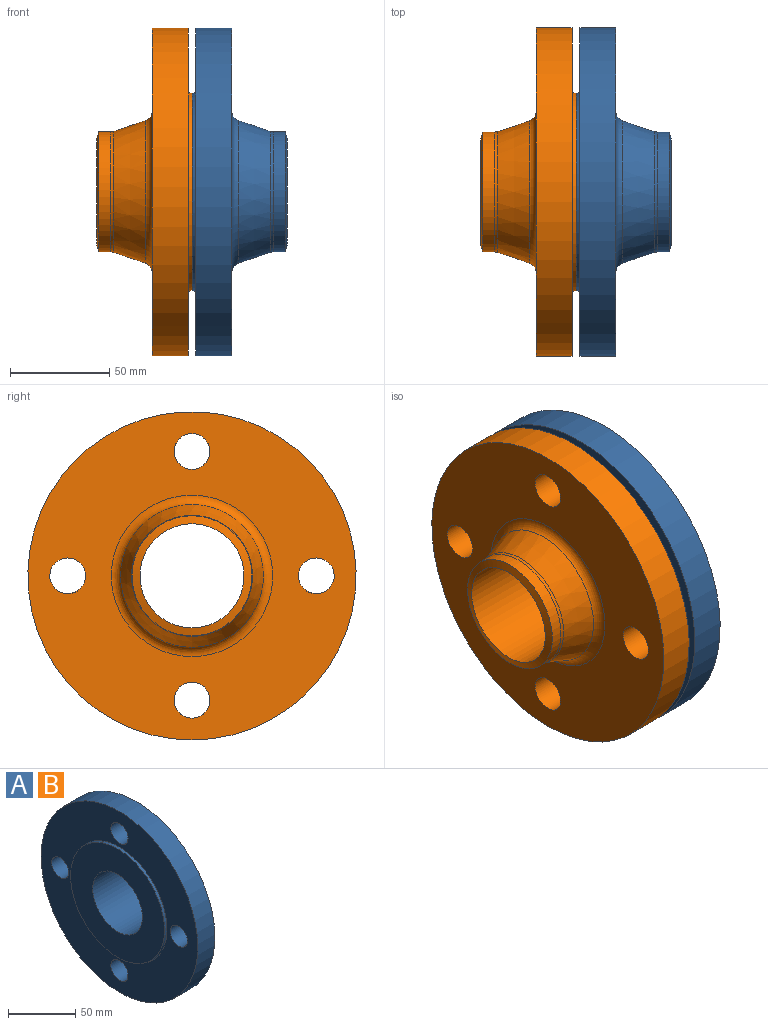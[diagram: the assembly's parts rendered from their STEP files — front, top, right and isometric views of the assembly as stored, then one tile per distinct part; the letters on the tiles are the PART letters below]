
ASSEMBLY  parts=2 mates=1
PART A: 15 faces, bbox 48x165x165 mm
  f0: plane 165x165mm, normal (1,0,0), area 15193.1mm2, adj f1,f10,f11,f12,f13,f14
  f1: torus R=40.57mm, axis (1,0,0), area 1475.4mm2, adj f0,f2
  f2: cone r=35.84mm half-angle=18.9deg, axis (-1,0,0), area 3483.8mm2, adj f1,f3
  f3: torus R=35.15mm, axis (1,0,0), area 313.5mm2, adj f2,f4
  f4: cylinder r=30.15mm len=60.3mm, axis (1,0,0), area 1154.8mm2, adj f3,f5
  f5: cone r=30.15mm half-angle=75deg, axis (-1,0,0), area 732.4mm2, adj f4,f7
  f6: plane 99x99mm, normal (-1,0,0), area 5549.4mm2, adj f7,f8
  f7: cylinder r=26.15mm len=52.3mm, axis (-1,0,0), area 7886.7mm2, adj f5,f6
  f8: cone r=49.5mm half-angle=15deg, axis (1,0,0), area 647.5mm2, adj f6,f9
  f9: plane 165x165mm, normal (-1,0,0), area 12499.3mm2, adj f8,f10,f11,f12,f13,f14
  f10: cylinder r=82.5mm len=165mm, axis (-1,0,0), area 9330.5mm2, adj f0,f9
  f11: cylinder r=9mm len=18mm, axis (-1,0,0), area 1017.9mm2, adj f0,f9
  f12: cylinder r=9mm len=18mm, axis (-1,0,0), area 1017.9mm2, adj f0,f9
  f13: cylinder r=9mm len=18mm, axis (-1,0,0), area 1017.9mm2, adj f0,f9
  f14: cylinder r=9mm len=18mm, axis (-1,0,0), area 1017.9mm2, adj f0,f9
PART B: same geometry as A
PLACE A t=(-23.11,-0.34,-1.09)mm
PLACE B rot(axis=(0,0,1),180deg) t=(-23.11,-0.34,-1.09)mm
MATE fastened B.f1 <-> A.f1  axis (1,0,0) through (-23.11,-0.34,-1.09)mm
